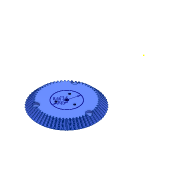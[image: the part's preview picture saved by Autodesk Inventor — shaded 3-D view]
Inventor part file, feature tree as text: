
AUTODESK INVENTOR PART (.ipt)
format: ipt  version: 2020.3 (Build 243373000, 373)  size: 1,558,528 bytes
history: native  units: mm
features: sketch x1, imported_body x1
ambient origin geometry x8: Origin, YZ Plane, XZ Plane, XY Plane, X Axis, Y Axis, Z Axis, Center Point
bodies: Solid1 (feature_tree)
feature tree (2):
  sketch  "Sketch1"  dims[d0=3.6mm d1=30.0mm d2=8.660254mm d3=10.0mm]
  imported_body  "Base1"
